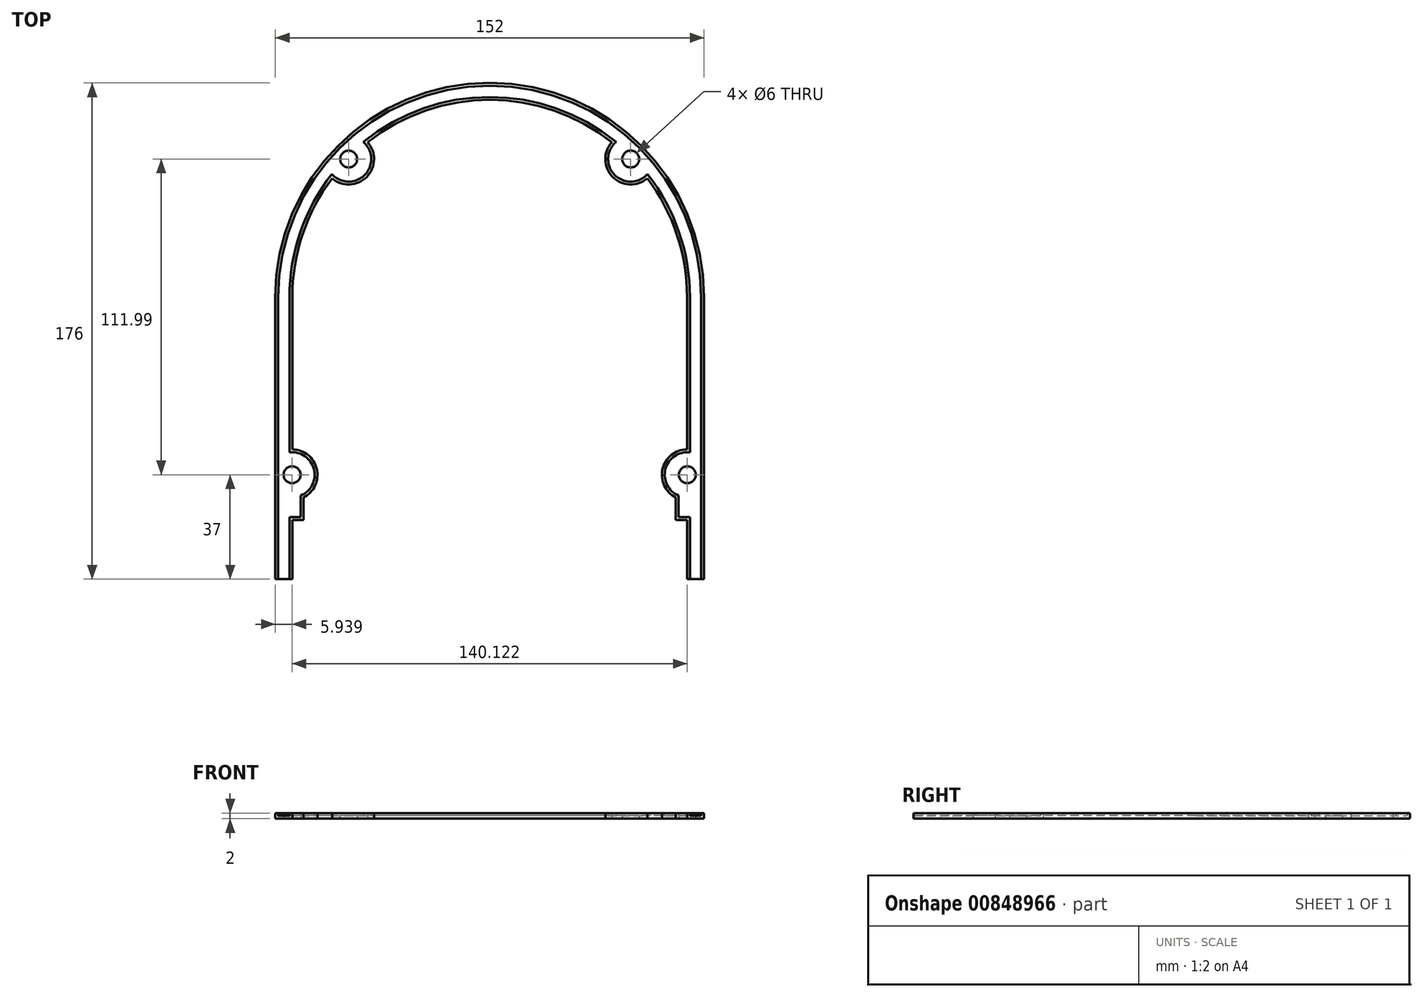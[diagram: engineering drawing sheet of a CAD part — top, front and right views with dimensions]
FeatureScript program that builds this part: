
annotation { "Feature Type Name" : "Feature", "Feature Type Description" : "" }
export const myFeature = defineFeature(function(context is Context, id is Id, definition is map)
    precondition{}
    {
        {
            var Q0;
            Q0=qCreatedBy(makeId("Top.planeOp"),FACE);
            var sketch = newSketch(context, id + "F0", { "sketchPlane" : qUnion([Q0])});
            skLineSegment(sketch, "E0.left", {"start": v(-76, 31) * mm, "end": v(-76, -31) * mm});
            skLineSegment(sketch, "E0.right", {"start": v(76, 31) * mm, "end": v(76, -31) * mm});
            skPoint(sketch, "E0.middle", {"position": v(0, 0) * mm});
            skLineSegment(sketch, "E1.left", {"start": v(-76, -31) * mm, "end": v(-76, -69) * mm});
            skLineSegment(sketch, "E1.right", {"start": v(76, -31) * mm, "end": v(76, -69) * mm});
            skArc(sketch, "E2", {"start": v(-76, 31) * mm, "mid": v(0, 107) * mm, "end": v(76, 31) * mm});
            skCircle(sketch, "E3", {"center": v(-50, 79.99) * mm, "radius": 3 * mm});
            skArc(sketch, "E4", {"start": v(-43.3, 86) * mm, "mid": v(-43.57, 73.7) * mm, "end": v(-55.87, 73.17) * mm});
            skCircle(sketch, "E5", {"center": v(-70.06, -32) * mm, "radius": 3 * mm});
            skLineSegment(sketch, "E6.left", {"start": v(-70, -69) * mm, "end": v(-70, -47.99) * mm});
            skLineSegment(sketch, "E7.bottom", {"start": v(-70, -47.99) * mm, "end": v(-66, -47.99) * mm});
            skArc(sketch, "E8", {"start": v(-66, -40.03) * mm, "mid": v(-61.3, -29.94) * mm, "end": v(-70, -23) * mm});
            skLineSegment(sketch, "E9", {"start": v(-70, 31) * mm, "end": v(-70, -23) * mm});
            skLineSegment(sketch, "E10", {"start": v(-66, -40.03) * mm, "end": v(-66, -47.99) * mm});
            skLineSegment(sketch, "E11", {"start": v(0, -75.5) * mm, "end": v(0, 119.6) * mm, "construction": true});
            skArc(sketch, "E12", {"start": v(-70, 31) * mm, "mid": v(-66.37, 53.24) * mm, "end": v(-55.87, 73.17) * mm});
            skArc(sketch, "E13", {"start": v(-43.3, 86) * mm, "mid": v(-22.91, 97.14) * mm, "end": v(0, 101) * mm});
            skArc(sketch, "E14.MirrorCS", {"start": v(43.3, 86) * mm, "mid": v(22.91, 97.14) * mm, "end": v(0, 101) * mm});
            skArc(sketch, "E15.MirrorCS", {"start": v(43.3, 86) * mm, "mid": v(43.57, 73.7) * mm, "end": v(55.87, 73.17) * mm});
            skCircle(sketch, "E16.MirrorC", {"center": v(50, 79.99) * mm, "radius": 3 * mm});
            skArc(sketch, "E17.MirrorCS", {"start": v(70, 31) * mm, "mid": v(66.37, 53.24) * mm, "end": v(55.87, 73.17) * mm});
            skLineSegment(sketch, "E18.MirrorCS", {"start": v(70, 31) * mm, "end": v(70, -23) * mm});
            skArc(sketch, "E19.MirrorCS", {"start": v(66, -40.03) * mm, "mid": v(61.3, -29.94) * mm, "end": v(70, -23) * mm});
            skCircle(sketch, "E20.MirrorC", {"center": v(70.06, -32) * mm, "radius": 3 * mm});
            skLineSegment(sketch, "E21.MirrorCS", {"start": v(66, -40.03) * mm, "end": v(66, -47.99) * mm});
            skLineSegment(sketch, "E22.MirrorCS", {"start": v(70, -47.99) * mm, "end": v(66, -47.99) * mm});
            skLineSegment(sketch, "E23.MirrorCS", {"start": v(70, -69) * mm, "end": v(70, -47.99) * mm});
            skLineSegment(sketch, "E24", {"start": v(-76, -69) * mm, "end": v(-70, -69) * mm});
            skLineSegment(sketch, "E25", {"start": v(70, -69) * mm, "end": v(76, -69) * mm});
            skSolve(sketch);
        }
        {
            var Q0;
            Q0=makeQuery(id+"F0.imprint","IMPRINT",FACE,{"disambiguationData":[TD([[makeQuery(id+"F0.imprint","IMPRINT",EDGE,{"derivedFrom":sQuery(id+"F0.wireOp",EDGE,"E0.left")}),1.0]])]});
            extrude(context, id + "F1", {"entities" : qUnion([Q0]), "depth" : 2 * mm, "offsetDistance" : 25 * mm});
        }
        {
            var Q0;
            Q0=makeQuery(id+"F1.opExtrude","CAP_FACE",FACE,{"disambiguationData":[OSD([sQuery(id+"F0.wireOp",EDGE,"E0.left"),sQuery(id+"F0.wireOp",EDGE,"E0.right"),sQuery(id+"F0.wireOp",EDGE,"E1.left"),sQuery(id+"F0.wireOp",EDGE,"E1.right"),sQuery(id+"F0.wireOp",EDGE,"E2"),sQuery(id+"F0.wireOp",EDGE,"E3"),sQuery(id+"F0.wireOp",EDGE,"E4"),sQuery(id+"F0.wireOp",EDGE,"E5"),sQuery(id+"F0.wireOp",EDGE,"E6.left"),sQuery(id+"F0.wireOp",EDGE,"E7.bottom"),sQuery(id+"F0.wireOp",EDGE,"E8"),sQuery(id+"F0.wireOp",EDGE,"E9"),sQuery(id+"F0.wireOp",EDGE,"E10"),sQuery(id+"F0.wireOp",EDGE,"E12"),sQuery(id+"F0.wireOp",EDGE,"E13"),sQuery(id+"F0.wireOp",EDGE,"E14.MirrorCS"),sQuery(id+"F0.wireOp",EDGE,"E15.MirrorCS"),sQuery(id+"F0.wireOp",EDGE,"E16.MirrorC"),sQuery(id+"F0.wireOp",EDGE,"E17.MirrorCS"),sQuery(id+"F0.wireOp",EDGE,"E18.MirrorCS"),sQuery(id+"F0.wireOp",EDGE,"E19.MirrorCS"),sQuery(id+"F0.wireOp",EDGE,"E20.MirrorC"),sQuery(id+"F0.wireOp",EDGE,"E21.MirrorCS"),sQuery(id+"F0.wireOp",EDGE,"E22.MirrorCS"),sQuery(id+"F0.wireOp",EDGE,"E23.MirrorCS"),sQuery(id+"F0.wireOp",EDGE,"E24"),sQuery(id+"F0.wireOp",EDGE,"E25")])],"isStart":false});
            shell(context, id + "F2", {"entities" : qUnion([Q0]), "thickness" : 1 * mm});
        }
        {
            var Q0;
            {var subQ0=sQuery(id+"F0.wireOp",EDGE,"E25");var subQ1=sQuery(id+"F0.wireOp",EDGE,"E24");var subQ2=sQuery(id+"F0.wireOp",EDGE,"E23.MirrorCS");var subQ3=sQuery(id+"F0.wireOp",EDGE,"E22.MirrorCS");var subQ4=sQuery(id+"F0.wireOp",EDGE,"E21.MirrorCS");var subQ5=sQuery(id+"F0.wireOp",EDGE,"E20.MirrorC");var subQ6=sQuery(id+"F0.wireOp",EDGE,"E19.MirrorCS");var subQ7=sQuery(id+"F0.wireOp",EDGE,"E18.MirrorCS");var subQ8=sQuery(id+"F0.wireOp",EDGE,"E17.MirrorCS");var subQ9=sQuery(id+"F0.wireOp",EDGE,"E16.MirrorC");var subQ10=sQuery(id+"F0.wireOp",EDGE,"E15.MirrorCS");var subQ11=sQuery(id+"F0.wireOp",EDGE,"E14.MirrorCS");var subQ12=sQuery(id+"F0.wireOp",EDGE,"E13");var subQ13=sQuery(id+"F0.wireOp",EDGE,"E12");var subQ14=sQuery(id+"F0.wireOp",EDGE,"E10");var subQ15=sQuery(id+"F0.wireOp",EDGE,"E9");var subQ16=sQuery(id+"F0.wireOp",EDGE,"E8");var subQ17=sQuery(id+"F0.wireOp",EDGE,"E7.bottom");var subQ18=sQuery(id+"F0.wireOp",EDGE,"E6.left");var subQ19=sQuery(id+"F0.wireOp",EDGE,"E5");var subQ20=sQuery(id+"F0.wireOp",EDGE,"E4");var subQ21=sQuery(id+"F0.wireOp",EDGE,"E3");var subQ22=sQuery(id+"F0.wireOp",EDGE,"E2");var subQ23=sQuery(id+"F0.wireOp",EDGE,"E1.right");var subQ24=sQuery(id+"F0.wireOp",EDGE,"E1.left");var subQ25=sQuery(id+"F0.wireOp",EDGE,"E0.right");var subQ26=sQuery(id+"F0.wireOp",EDGE,"E0.left");Q0=makeQuery(id+"F2.opShell","OFFSET_FACE",FACE,{"disambiguationData":[OSD([subQ26,subQ25,subQ24,subQ23,subQ22,subQ21,subQ20,subQ19,subQ18,subQ17,subQ16,subQ15,subQ14,subQ13,subQ12,subQ11,subQ10,subQ9,subQ8,subQ7,subQ6,subQ5,subQ4,subQ3,subQ2,subQ1,subQ0]),TDD([makeQuery(id+"F1.opExtrude","CAP_FACE",FACE,{"disambiguationData":[OSD([subQ26,subQ25,subQ24,subQ23,subQ22,subQ21,subQ20,subQ19,subQ18,subQ17,subQ16,subQ15,subQ14,subQ13,subQ12,subQ11,subQ10,subQ9,subQ8,subQ7,subQ6,subQ5,subQ4,subQ3,subQ2,subQ1,subQ0])],"isStart":false})]),OD(0.0)]});}
            var Q1;
            {var subQ0=sQuery(id+"F0.wireOp",EDGE,"E25");var subQ1=sQuery(id+"F0.wireOp",EDGE,"E24");var subQ2=sQuery(id+"F0.wireOp",EDGE,"E23.MirrorCS");var subQ3=sQuery(id+"F0.wireOp",EDGE,"E22.MirrorCS");var subQ4=sQuery(id+"F0.wireOp",EDGE,"E21.MirrorCS");var subQ5=sQuery(id+"F0.wireOp",EDGE,"E20.MirrorC");var subQ6=sQuery(id+"F0.wireOp",EDGE,"E19.MirrorCS");var subQ7=sQuery(id+"F0.wireOp",EDGE,"E18.MirrorCS");var subQ8=sQuery(id+"F0.wireOp",EDGE,"E17.MirrorCS");var subQ9=sQuery(id+"F0.wireOp",EDGE,"E16.MirrorC");var subQ10=sQuery(id+"F0.wireOp",EDGE,"E15.MirrorCS");var subQ11=sQuery(id+"F0.wireOp",EDGE,"E14.MirrorCS");var subQ12=sQuery(id+"F0.wireOp",EDGE,"E13");var subQ13=sQuery(id+"F0.wireOp",EDGE,"E12");var subQ14=sQuery(id+"F0.wireOp",EDGE,"E10");var subQ15=sQuery(id+"F0.wireOp",EDGE,"E9");var subQ16=sQuery(id+"F0.wireOp",EDGE,"E8");var subQ17=sQuery(id+"F0.wireOp",EDGE,"E7.bottom");var subQ18=sQuery(id+"F0.wireOp",EDGE,"E6.left");var subQ19=sQuery(id+"F0.wireOp",EDGE,"E5");var subQ20=sQuery(id+"F0.wireOp",EDGE,"E4");var subQ21=sQuery(id+"F0.wireOp",EDGE,"E3");var subQ22=sQuery(id+"F0.wireOp",EDGE,"E2");var subQ23=sQuery(id+"F0.wireOp",EDGE,"E1.right");var subQ24=sQuery(id+"F0.wireOp",EDGE,"E1.left");var subQ25=sQuery(id+"F0.wireOp",EDGE,"E0.right");var subQ26=sQuery(id+"F0.wireOp",EDGE,"E0.left");Q1=makeQuery(id+"F2.opShell","OFFSET_FACE",FACE,{"disambiguationData":[OSD([subQ26,subQ25,subQ24,subQ23,subQ22,subQ21,subQ20,subQ19,subQ18,subQ17,subQ16,subQ15,subQ14,subQ13,subQ12,subQ11,subQ10,subQ9,subQ8,subQ7,subQ6,subQ5,subQ4,subQ3,subQ2,subQ1,subQ0]),TDD([makeQuery(id+"F1.opExtrude","CAP_FACE",FACE,{"disambiguationData":[OSD([subQ26,subQ25,subQ24,subQ23,subQ22,subQ21,subQ20,subQ19,subQ18,subQ17,subQ16,subQ15,subQ14,subQ13,subQ12,subQ11,subQ10,subQ9,subQ8,subQ7,subQ6,subQ5,subQ4,subQ3,subQ2,subQ1,subQ0])],"isStart":false})]),OD(1.0)]});}
            var Q2;
            {var subQ0=sQuery(id+"F0.wireOp",EDGE,"E25");var subQ1=sQuery(id+"F0.wireOp",EDGE,"E24");var subQ2=sQuery(id+"F0.wireOp",EDGE,"E23.MirrorCS");var subQ3=sQuery(id+"F0.wireOp",EDGE,"E22.MirrorCS");var subQ4=sQuery(id+"F0.wireOp",EDGE,"E21.MirrorCS");var subQ5=sQuery(id+"F0.wireOp",EDGE,"E20.MirrorC");var subQ6=sQuery(id+"F0.wireOp",EDGE,"E19.MirrorCS");var subQ7=sQuery(id+"F0.wireOp",EDGE,"E18.MirrorCS");var subQ8=sQuery(id+"F0.wireOp",EDGE,"E17.MirrorCS");var subQ9=sQuery(id+"F0.wireOp",EDGE,"E16.MirrorC");var subQ10=sQuery(id+"F0.wireOp",EDGE,"E15.MirrorCS");var subQ11=sQuery(id+"F0.wireOp",EDGE,"E14.MirrorCS");var subQ12=sQuery(id+"F0.wireOp",EDGE,"E13");var subQ13=sQuery(id+"F0.wireOp",EDGE,"E12");var subQ14=sQuery(id+"F0.wireOp",EDGE,"E10");var subQ15=sQuery(id+"F0.wireOp",EDGE,"E9");var subQ16=sQuery(id+"F0.wireOp",EDGE,"E8");var subQ17=sQuery(id+"F0.wireOp",EDGE,"E7.bottom");var subQ18=sQuery(id+"F0.wireOp",EDGE,"E6.left");var subQ19=sQuery(id+"F0.wireOp",EDGE,"E5");var subQ20=sQuery(id+"F0.wireOp",EDGE,"E4");var subQ21=sQuery(id+"F0.wireOp",EDGE,"E3");var subQ22=sQuery(id+"F0.wireOp",EDGE,"E2");var subQ23=sQuery(id+"F0.wireOp",EDGE,"E1.right");var subQ24=sQuery(id+"F0.wireOp",EDGE,"E1.left");var subQ25=sQuery(id+"F0.wireOp",EDGE,"E0.right");var subQ26=sQuery(id+"F0.wireOp",EDGE,"E0.left");Q2=makeQuery(id+"F2.opShell","OFFSET_FACE",FACE,{"disambiguationData":[OSD([subQ26,subQ25,subQ24,subQ23,subQ22,subQ21,subQ20,subQ19,subQ18,subQ17,subQ16,subQ15,subQ14,subQ13,subQ12,subQ11,subQ10,subQ9,subQ8,subQ7,subQ6,subQ5,subQ4,subQ3,subQ2,subQ1,subQ0]),TDD([makeQuery(id+"F1.opExtrude","CAP_FACE",FACE,{"disambiguationData":[OSD([subQ26,subQ25,subQ24,subQ23,subQ22,subQ21,subQ20,subQ19,subQ18,subQ17,subQ16,subQ15,subQ14,subQ13,subQ12,subQ11,subQ10,subQ9,subQ8,subQ7,subQ6,subQ5,subQ4,subQ3,subQ2,subQ1,subQ0])],"isStart":false})]),OD(3.0)]});}
            var Q3;
            {var subQ0=sQuery(id+"F0.wireOp",EDGE,"E25");var subQ1=sQuery(id+"F0.wireOp",EDGE,"E24");var subQ2=sQuery(id+"F0.wireOp",EDGE,"E23.MirrorCS");var subQ3=sQuery(id+"F0.wireOp",EDGE,"E22.MirrorCS");var subQ4=sQuery(id+"F0.wireOp",EDGE,"E21.MirrorCS");var subQ5=sQuery(id+"F0.wireOp",EDGE,"E20.MirrorC");var subQ6=sQuery(id+"F0.wireOp",EDGE,"E19.MirrorCS");var subQ7=sQuery(id+"F0.wireOp",EDGE,"E18.MirrorCS");var subQ8=sQuery(id+"F0.wireOp",EDGE,"E17.MirrorCS");var subQ9=sQuery(id+"F0.wireOp",EDGE,"E16.MirrorC");var subQ10=sQuery(id+"F0.wireOp",EDGE,"E15.MirrorCS");var subQ11=sQuery(id+"F0.wireOp",EDGE,"E14.MirrorCS");var subQ12=sQuery(id+"F0.wireOp",EDGE,"E13");var subQ13=sQuery(id+"F0.wireOp",EDGE,"E12");var subQ14=sQuery(id+"F0.wireOp",EDGE,"E10");var subQ15=sQuery(id+"F0.wireOp",EDGE,"E9");var subQ16=sQuery(id+"F0.wireOp",EDGE,"E8");var subQ17=sQuery(id+"F0.wireOp",EDGE,"E7.bottom");var subQ18=sQuery(id+"F0.wireOp",EDGE,"E6.left");var subQ19=sQuery(id+"F0.wireOp",EDGE,"E5");var subQ20=sQuery(id+"F0.wireOp",EDGE,"E4");var subQ21=sQuery(id+"F0.wireOp",EDGE,"E3");var subQ22=sQuery(id+"F0.wireOp",EDGE,"E2");var subQ23=sQuery(id+"F0.wireOp",EDGE,"E1.right");var subQ24=sQuery(id+"F0.wireOp",EDGE,"E1.left");var subQ25=sQuery(id+"F0.wireOp",EDGE,"E0.right");var subQ26=sQuery(id+"F0.wireOp",EDGE,"E0.left");Q3=makeQuery(id+"F2.opShell","OFFSET_FACE",FACE,{"disambiguationData":[OSD([subQ26,subQ25,subQ24,subQ23,subQ22,subQ21,subQ20,subQ19,subQ18,subQ17,subQ16,subQ15,subQ14,subQ13,subQ12,subQ11,subQ10,subQ9,subQ8,subQ7,subQ6,subQ5,subQ4,subQ3,subQ2,subQ1,subQ0]),TDD([makeQuery(id+"F1.opExtrude","CAP_FACE",FACE,{"disambiguationData":[OSD([subQ26,subQ25,subQ24,subQ23,subQ22,subQ21,subQ20,subQ19,subQ18,subQ17,subQ16,subQ15,subQ14,subQ13,subQ12,subQ11,subQ10,subQ9,subQ8,subQ7,subQ6,subQ5,subQ4,subQ3,subQ2,subQ1,subQ0])],"isStart":false})]),OD(2.0)]});}
            extrude(context, id + "F3", {"entities" : qUnion([Q0, Q1, Q2, Q3]), "operationType" : NewBodyOperationType.REMOVE, "oppositeDirection" : true, "depth" : 1 * mm, "offsetDistance" : 25 * mm});
        }
        {
            var Q0;
            Q0=makeQuery(id+"F1.opExtrude","CAP_FACE",FACE,{"disambiguationData":[OSD([sQuery(id+"F0.wireOp",EDGE,"E0.left"),sQuery(id+"F0.wireOp",EDGE,"E0.right"),sQuery(id+"F0.wireOp",EDGE,"E1.left"),sQuery(id+"F0.wireOp",EDGE,"E1.right"),sQuery(id+"F0.wireOp",EDGE,"E2"),sQuery(id+"F0.wireOp",EDGE,"E3"),sQuery(id+"F0.wireOp",EDGE,"E4"),sQuery(id+"F0.wireOp",EDGE,"E5"),sQuery(id+"F0.wireOp",EDGE,"E6.left"),sQuery(id+"F0.wireOp",EDGE,"E7.bottom"),sQuery(id+"F0.wireOp",EDGE,"E8"),sQuery(id+"F0.wireOp",EDGE,"E9"),sQuery(id+"F0.wireOp",EDGE,"E10"),sQuery(id+"F0.wireOp",EDGE,"E12"),sQuery(id+"F0.wireOp",EDGE,"E13"),sQuery(id+"F0.wireOp",EDGE,"E14.MirrorCS"),sQuery(id+"F0.wireOp",EDGE,"E15.MirrorCS"),sQuery(id+"F0.wireOp",EDGE,"E16.MirrorC"),sQuery(id+"F0.wireOp",EDGE,"E17.MirrorCS"),sQuery(id+"F0.wireOp",EDGE,"E18.MirrorCS"),sQuery(id+"F0.wireOp",EDGE,"E19.MirrorCS"),sQuery(id+"F0.wireOp",EDGE,"E20.MirrorC"),sQuery(id+"F0.wireOp",EDGE,"E21.MirrorCS"),sQuery(id+"F0.wireOp",EDGE,"E22.MirrorCS"),sQuery(id+"F0.wireOp",EDGE,"E23.MirrorCS"),sQuery(id+"F0.wireOp",EDGE,"E24"),sQuery(id+"F0.wireOp",EDGE,"E25")])],"isStart":false});
            var sketch = newSketch(context, id + "F4", { "sketchPlane" : qUnion([Q0])});
            skLineSegment(sketch, "E26.bottom", {"start": v(71, -68) * mm, "end": v(75, -68) * mm});
            skLineSegment(sketch, "E26.top", {"start": v(71, -69) * mm, "end": v(75, -69) * mm});
            skLineSegment(sketch, "E26.left", {"start": v(71, -68) * mm, "end": v(71, -69) * mm});
            skLineSegment(sketch, "E26.right", {"start": v(75, -68) * mm, "end": v(75, -69) * mm});
            skLineSegment(sketch, "E27.bottom", {"start": v(-75, -68) * mm, "end": v(-71, -68) * mm});
            skLineSegment(sketch, "E27.top", {"start": v(-75, -69) * mm, "end": v(-71, -69) * mm});
            skLineSegment(sketch, "E27.left", {"start": v(-75, -68) * mm, "end": v(-75, -69) * mm});
            skLineSegment(sketch, "E27.right", {"start": v(-71, -68) * mm, "end": v(-71, -69) * mm});
            skSolve(sketch);
        }
        {
            var Q0;
            Q0=makeQuery(id+"F4.imprint","IMPRINT",FACE,{"disambiguationData":[TD([[makeQuery(id+"F4.imprint","IMPRINT",EDGE,{"derivedFrom":sQuery(id+"F4.wireOp",EDGE,"E27.bottom")}),-1.0]])]});
            var Q1;
            Q1=makeQuery(id+"F4.imprint","IMPRINT",FACE,{"disambiguationData":[TD([[makeQuery(id+"F4.imprint","IMPRINT",EDGE,{"derivedFrom":sQuery(id+"F4.wireOp",EDGE,"E26.bottom")}),-1.0]])]});
            extrude(context, id + "F5", {"entities" : qUnion([Q0, Q1]), "operationType" : NewBodyOperationType.REMOVE, "oppositeDirection" : true, "depth" : 1 * mm, "offsetDistance" : 25 * mm});
        }
    });
